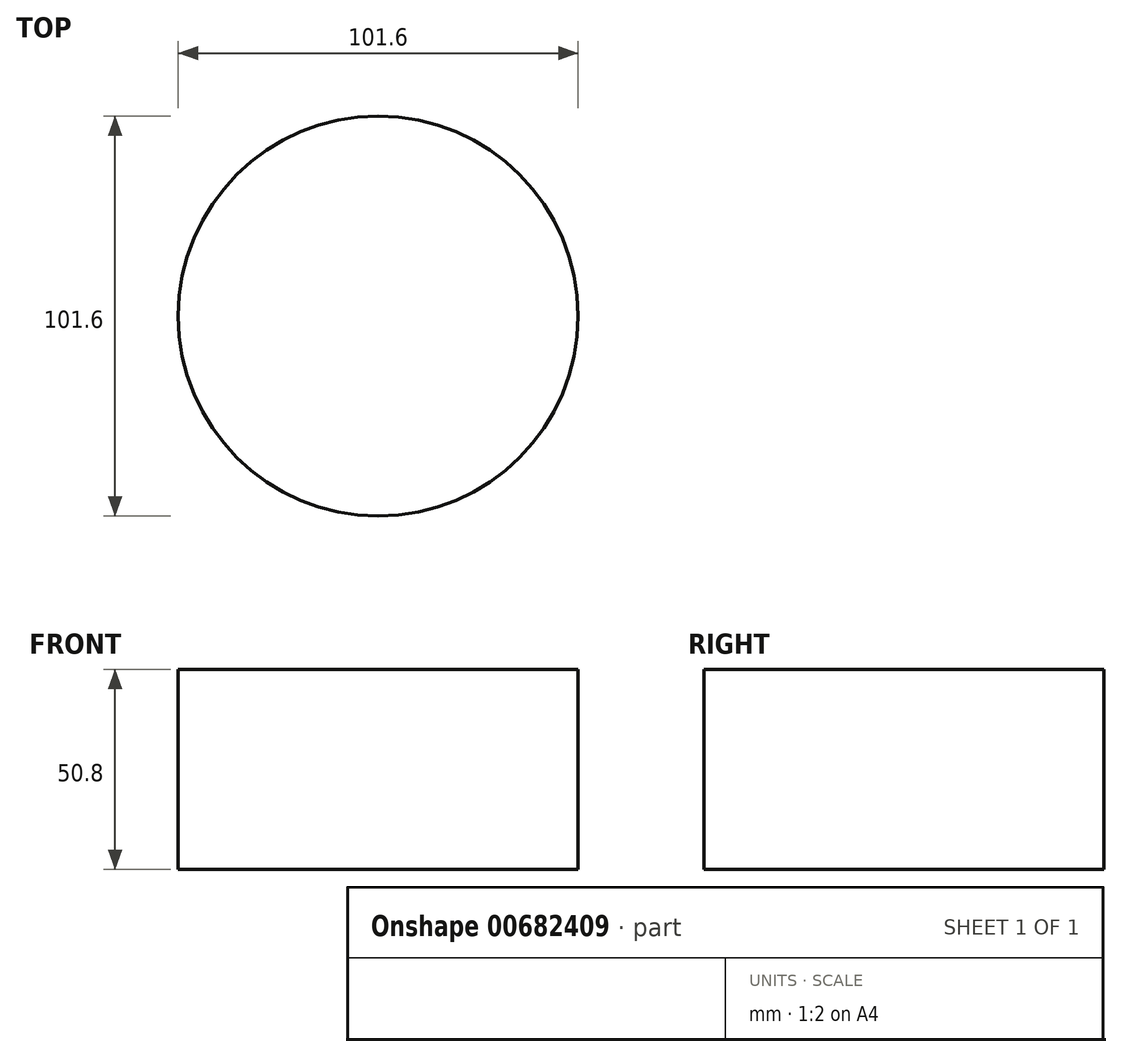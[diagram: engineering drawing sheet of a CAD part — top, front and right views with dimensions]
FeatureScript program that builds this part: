
annotation { "Feature Type Name" : "Feature", "Feature Type Description" : "" }
export const myFeature = defineFeature(function(context is Context, id is Id, definition is map)
    precondition{}
    {
        {
            var Q0;
            Q0=qCreatedBy(makeId("Top.planeOp"),FACE);
            var sketch = newSketch(context, id + "F0", { "sketchPlane" : qUnion([Q0])});
            skCircle(sketch, "E0", {"center": v(0, 0) * mm, "radius": 50.8 * mm});
            skSolve(sketch);
        }
        {
            var Q0;
            Q0=makeQuery(id+"F0.imprint","IMPRINT",FACE,{"disambiguationData":[TD([[makeQuery(id+"F0.imprint","IMPRINT",EDGE,{"derivedFrom":sQuery(id+"F0.wireOp",EDGE,"E0")}),1.0]])]});
            extrude(context, id + "F1", {"entities" : qUnion([Q0]), "depth" : 50.8 * mm, "offsetDistance" : 25.4 * mm});
        }
    });
